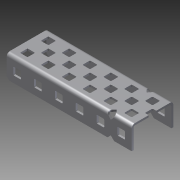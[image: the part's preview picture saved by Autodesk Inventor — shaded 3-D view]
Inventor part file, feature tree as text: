
AUTODESK INVENTOR PART (.ipt)
format: ipt  version: 2012 (Build 160160000, 160)  size: 564,736 bytes
history: native  units: in
note: dims shown in document units (in); Inventor stores cm internally (conversion verified against a paired STEP export)
features: other x1, imported_body x1, plane x1, split x1
ambient origin geometry x8: Origin, YZ Plane, XZ Plane, XY Plane, X Axis, Y Axis, Z Axis, Center Point
feature tree (4):
  parser-record x1  (decoder bookkeeping rows leaked as tree rows — omitted from the tree; the rows remain in map.json)
  imported_body  "Base1"
  plane  "Work Plane1"
  split  "Split1"
